# Revit family: 44569573(2021)
name_source: partatom
category: Plumbing Fixtures
units: mm (PartAtom-declared; Revit-internal decimal feet)

## family parameters
Always vertical = Yes
Cut with Voids When Loaded = No
OmniClass Number = 23.45.55.00
OmniClass Title = Sanitary Faucets, Wastes
Part Type = Normal
Room Calculation Point = No
Round Connector Dimension = Use Diameter
Shared = No
Work Plane-Based = No

## types (1)
- 44569573 Cover part for shower faucet
    2D/3D/BIM Files URL = http://static.hansa.com
    3D View = https://static.hansa.com
    Advanced Features = Inner body made of DZR brass
    AssetType = Fixed
    BIMObjectName = 44569573(2021)
    Backflow Prevention EN1717 = EB
    BodyMaterial = Brass
    Brand = HANSA
    Catalog Drawing URL = http://static.hansa.com
    Category = Shower solutions
    CloseOffRating = 0
    Color = Chrome
    Concealed Parts = Square rosette;Sleeve
    Connection Size = G1/2
    Default Elevation = 0 mm  [stored 0 ft]
    Dimension Drawing URL = http://static.hansa.com
    DurationUnit = Year
    EAN Number = 4057304015281
    EN Standard = EN 817
    ETIM Class Number = EC010546 Mechanical control system for shower
    FDV Document URL = http://www.hansa.com
    FaucetMainMaterial = Brass
    Features = Trim Kit;Single-lever
    Finish = Polished
    Flow Drawing URL = http://static.hansa.com
    Flow Rate At 300kPa = 0.0 L/s
    FlowCoefficient = 0
    Group = Shower faucet
    IfcExportAs = IfcValveType
    IfcExportType = FAUCET
    Installation Type = Concealed wall mounting
    Installation and Maintenance Guide URL = http://static.hansa.com
    Interactive AR View URL = https://static.hansa.com
    Lever Handle = Single operating lever/handle;Hot/Cold symbols
    Manufacturer = HANSA
    ManufacturerName = HANSA
    ManufacturerURL = http://www.hansa.com
    Market = International;Germany;Austria;Belgium;Netherlands;France;Czech Republic;Slovakia;Italy;Spain
    Material = Brass
    Max. Hot Water Supply = 80 °C
    Mechanical Parts = ø 40 mm ceramic cartridge for flow and temperature control
    Mobile Product Information URL = http://mpi.hansa.com
    Model = 44569573 Cover part for shower faucet
    ModelReference = 44569573
    NBSDescription = Shower mixers
    NBSReference = 45-35-70/335
    Name = 44569573 Cover part for shower faucet
    Name_en = 44569573 Cover part for shower faucet
    Noise Class = II (ISO 3822)
    NominalDepth = 87 mm
    NominalHeight = 105 mm
    NominalWidth = 175 mm  [stored 0.574147 ft]
    Product Code = 44569573
    Product Family = HANSASTELA
    Product Image URL = http://static.hansa.com
    Product URL = http://static.hansa.com
    Sales Package dimensions (LxWxH) = 210 x 208 x 85
    Shape = Sculptured
    Size = 175x85x105 mm
    Spare-Part Information URL = http://static.hansa.com
    Surface treatment = Chrome
    Technical DataSheet URL = http://www.hansa.com
    UNSPSC Class Number = 30181810 Faucet trim
    URL Declaration Of Performance (DOP) = http://static.hansa.com
    URL Declaration of Asbestos = http://static.hansa.com
    URL Declaration of Conformity = http://static.hansa.com
    URL Declaration of SCIP = http://static.hansa.com
    URL EU Packaging Declaration = http://static.hansa.com
    URL EcoLabel Declaration = http://static.hansa.com
    URL REACH = http://static.hansa.com
    URL UWL = http://static.hansa.com
    Uniclass2 = Pr_40_30_96_78
    Uniclass2015Description = Shower manual water supply sets
    Uniclass2015Reference = Pr_40_20_87_78
    Version = 1
    VersionDate = 01/06/2023
    Warranty Information URL = http://warranty.hansa.com
    WarrantyDescription = http://warranty.hansa.com
    WarrantyDurationUnit = Year
    Working Pressure = 50 - 1000 kPa

note: [stored X ft] marks values corroborated as IEEE doubles in the binary element streams (Revit-internal decimal feet)

## geometry (parser evidence)
native form markers: Sweep x7
no freeform markers — native parametric forms only
